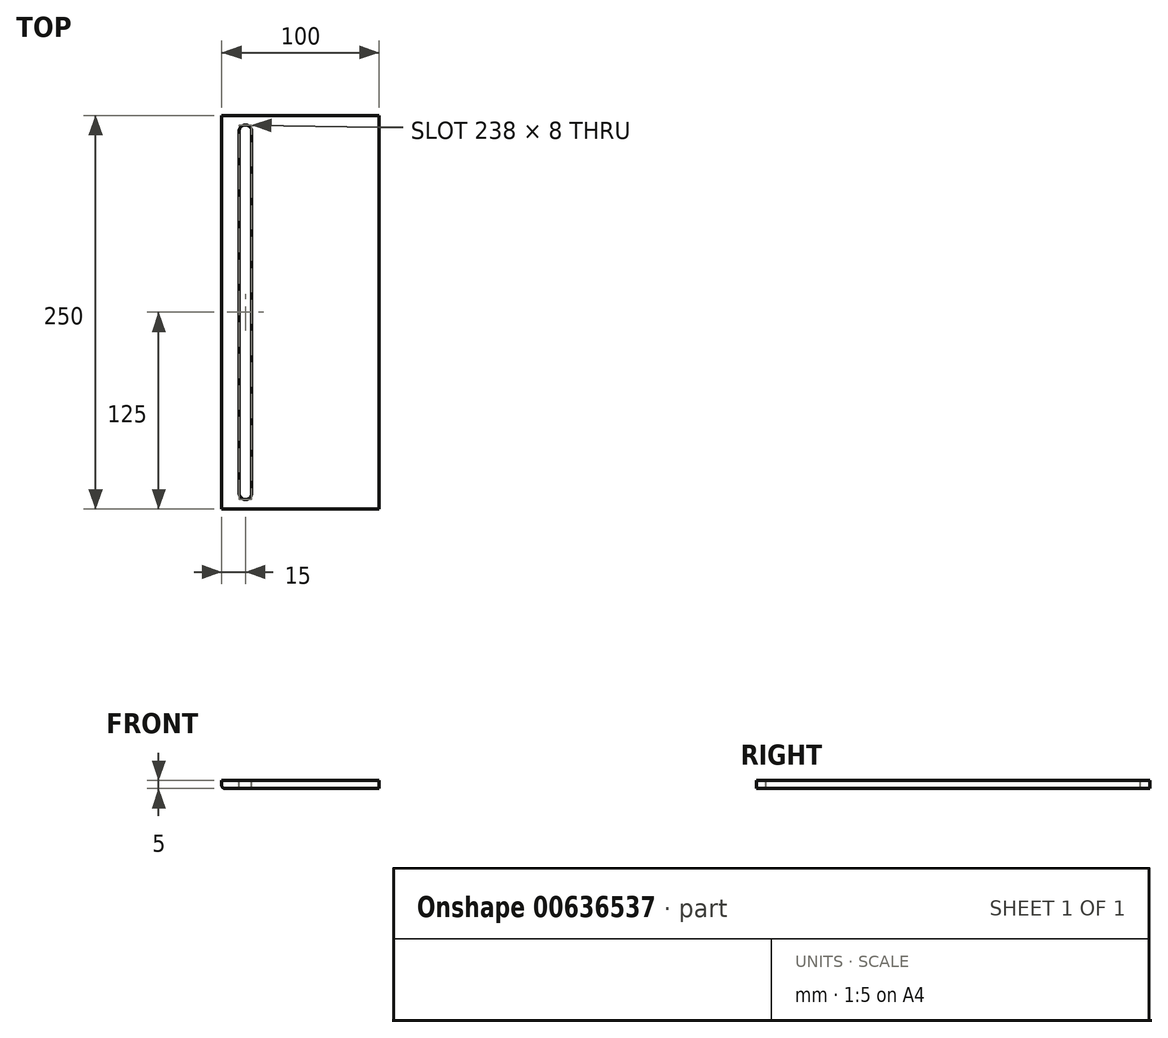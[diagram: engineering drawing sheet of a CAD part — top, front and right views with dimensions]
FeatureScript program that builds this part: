
annotation { "Feature Type Name" : "Feature", "Feature Type Description" : "" }
export const myFeature = defineFeature(function(context is Context, id is Id, definition is map)
    precondition{}
    {
        {
            var Q0;
            Q0=qCreatedBy(makeId("Top.planeOp"),FACE);
            var sketch = newSketch(context, id + "F0", { "sketchPlane" : qUnion([Q0])});
            skLineSegment(sketch, "E0.bottom", {"start": v(-50, 125) * mm, "end": v(50, 125) * mm});
            skLineSegment(sketch, "E0.top", {"start": v(-50, -125) * mm, "end": v(50, -125) * mm});
            skLineSegment(sketch, "E0.left", {"start": v(-50, 125) * mm, "end": v(-50, -125) * mm});
            skLineSegment(sketch, "E0.right", {"start": v(50, 125) * mm, "end": v(50, -125) * mm});
            skPoint(sketch, "E0.middle", {"position": v(0, 0) * mm});
            skSolve(sketch);
        }
        {
            var Q0;
            Q0=makeQuery(id+"F0.imprint","IMPRINT",FACE,{"disambiguationData":[TD([[makeQuery(id+"F0.imprint","IMPRINT",EDGE,{"derivedFrom":sQuery(id+"F0.wireOp",EDGE,"E0.bottom")}),-1.0]])]});
            extrude(context, id + "F1", {"entities" : qUnion([Q0]), "depth" : 5 * mm, "offsetDistance" : 25 * mm});
        }
        {
            var Q0;
            Q0=makeQuery(id+"F1.opExtrude","CAP_FACE",FACE,{"disambiguationData":[OSD([sQuery(id+"F0.wireOp",EDGE,"E0.bottom"),sQuery(id+"F0.wireOp",EDGE,"E0.top"),sQuery(id+"F0.wireOp",EDGE,"E0.left"),sQuery(id+"F0.wireOp",EDGE,"E0.right")])],"isStart":false});
            var sketch = newSketch(context, id + "F2", { "sketchPlane" : qUnion([Q0])});
            skLineSegment(sketch, "E1.0.0", {"start": v(-50, 125) * mm, "end": v(-50, -125) * mm});
            skLineSegment(sketch, "E1.0.1", {"start": v(-50, -125) * mm, "end": v(50, -125) * mm});
            skLineSegment(sketch, "E1.0.2", {"start": v(50, -125) * mm, "end": v(50, 125) * mm});
            skLineSegment(sketch, "E1.0.3", {"start": v(50, 125) * mm, "end": v(-50, 125) * mm});
            skLineSegment(sketch, "E2", {"start": v(-50, 0) * mm, "end": v(50, 0) * mm, "construction": true});
            skLineSegment(sketch, "E3", {"start": v(0, -125) * mm, "end": v(0, 125) * mm, "construction": true});
            skLineSegment(sketch, "E4", {"start": v(-35, 125) * mm, "end": v(-35, -125) * mm, "construction": true});
            skLineSegment(sketch, "E5.bottom", {"start": v(-39, 115) * mm, "end": v(-31, 115) * mm});
            skLineSegment(sketch, "E5.top", {"start": v(-39, -115) * mm, "end": v(-31, -115) * mm});
            skLineSegment(sketch, "E5.left", {"start": v(-39, 115) * mm, "end": v(-39, -115) * mm});
            skLineSegment(sketch, "E5.right", {"start": v(-31, 115) * mm, "end": v(-31, -115) * mm});
            skPoint(sketch, "E5.middle", {"position": v(-35, 0) * mm});
            skArc(sketch, "E6", {"start": v(-31, 115) * mm, "mid": v(-35, 119) * mm, "end": v(-39, 115) * mm});
            skArc(sketch, "E7", {"start": v(-39, -115) * mm, "mid": v(-35, -119) * mm, "end": v(-31, -115) * mm});
            skSolve(sketch);
        }
        {
            var Q0;
            Q0=makeQuery(id+"F1.opExtrude","CAP_EDGE",EDGE,{"disambiguationData":[OSD([sQuery(id+"F0.wireOp",EDGE,"E0.left")])],"isStart":true});
            fillet(context, id + "F3", {"entities" : qUnion([Q0]), "radius" : 2 * mm, "tangentPropagation" : true, "allowEdgeOverflow" : false});
        }
        {
            var Q0;
            Q0=makeQuery(id+"F2.imprint","IMPRINT",FACE,{"disambiguationData":[TD([[makeQuery(id+"F2.imprint","IMPRINT",EDGE,{"derivedFrom":sQuery(id+"F2.wireOp",EDGE,"E5.bottom")}),-1.0]])]});
            var Q1;
            Q1=makeQuery(id+"F2.imprint","IMPRINT",FACE,{"disambiguationData":[TD([[makeQuery(id+"F2.imprint","IMPRINT",EDGE,{"derivedFrom":sQuery(id+"F2.wireOp",EDGE,"E5.bottom")}),1.0]])]});
            var Q2;
            Q2=makeQuery(id+"F2.imprint","IMPRINT",FACE,{"disambiguationData":[TD([[makeQuery(id+"F2.imprint","IMPRINT",EDGE,{"derivedFrom":sQuery(id+"F2.wireOp",EDGE,"E5.top")}),-1.0]])]});
            extrude(context, id + "F4", {"entities" : qUnion([Q0, Q1, Q2]), "operationType" : NewBodyOperationType.REMOVE, "oppositeDirection" : true, "depth" : 25 * mm, "offsetDistance" : 25 * mm});
        }
    });
